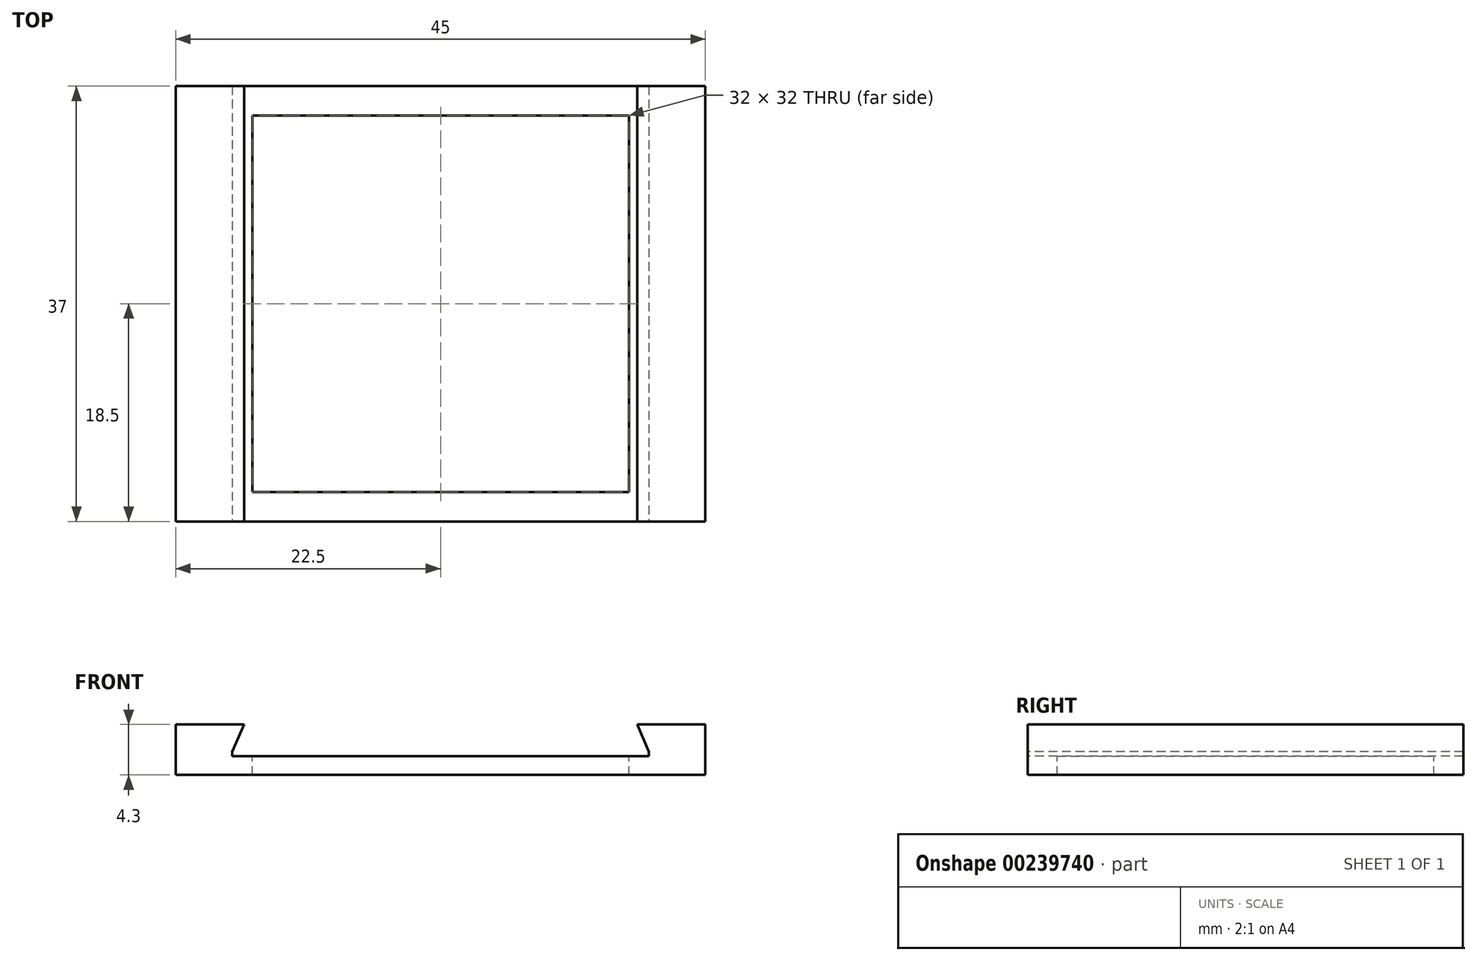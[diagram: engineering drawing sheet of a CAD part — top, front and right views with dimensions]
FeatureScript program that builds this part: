
annotation { "Feature Type Name" : "Feature", "Feature Type Description" : "" }
export const myFeature = defineFeature(function(context is Context, id is Id, definition is map)
    precondition{}
    {
        {
            var Q0;
            Q0=qCreatedBy(makeId("Top.planeOp"),FACE);
            var sketch = newSketch(context, id + "F0", { "sketchPlane" : qUnion([Q0])});
            skLineSegment(sketch, "E0.bottom", {"start": v(22.5, -18.5) * mm, "end": v(-22.5, -18.5) * mm});
            skLineSegment(sketch, "E0.top", {"start": v(22.5, 18.5) * mm, "end": v(-22.5, 18.5) * mm});
            skLineSegment(sketch, "E0.left", {"start": v(22.5, -18.5) * mm, "end": v(22.5, 18.5) * mm});
            skLineSegment(sketch, "E0.right", {"start": v(-22.5, -18.5) * mm, "end": v(-22.5, 18.5) * mm});
            skPoint(sketch, "E0.middle", {"position": v(0, 0) * mm});
            skSolve(sketch);
        }
        {
            var Q0;
            Q0=qSketchRegion(id+"F0",true);
            extrude(context, id + "F1", {"entities" : qUnion([Q0]), "depth" : 8 * mm});
        }
        {
            var Q0;
            Q0=makeQuery(id+"F1.opExtrude","SWEPT_FACE",FACE,{"disambiguationData":[OSD([sQuery(id+"F0.wireOp",EDGE,"E0.bottom")])]});
            var sketch = newSketch(context, id + "F2", { "sketchPlane" : qUnion([Q0])});
            skLineSegment(sketch, "E1", {"start": v(-22.5, 3) * mm, "end": v(22.5, 3) * mm, "construction": true});
            skLineSegment(sketch, "E2", {"start": v(-17.7, 8) * mm, "end": v(-17.7, 0) * mm, "construction": true});
            skLineSegment(sketch, "E3", {"start": v(0, 13.1) * mm, "end": v(0, -6.27) * mm, "construction": true});
            skLineSegment(sketch, "E4.MirrorCS", {"start": v(17.7, 8) * mm, "end": v(17.7, 0) * mm, "construction": true});
            skLineSegment(sketch, "E5", {"start": v(-15.7, 8) * mm, "end": v(-15.7, 0) * mm, "construction": true});
            skLineSegment(sketch, "E6", {"start": v(-15.7, 8) * mm, "end": v(15.7, 8) * mm});
            skLineSegment(sketch, "E7", {"start": v(-17.7, 3) * mm, "end": v(17.7, 3) * mm});
            skLineSegment(sketch, "E8", {"start": v(-17.7, 3) * mm, "end": v(-17.7, 3.4) * mm});
            skLineSegment(sketch, "E9", {"start": v(-17.7, 3.4) * mm, "end": v(-15.7, 8) * mm});
            skLineSegment(sketch, "E10.MirrorCS", {"start": v(17.7, 3.4) * mm, "end": v(15.7, 8) * mm});
            skLineSegment(sketch, "E11", {"start": v(17.7, 3.4) * mm, "end": v(17.7, 3) * mm});
            skSolve(sketch);
        }
        {
            var Q0;
            Q0=qSketchRegion(id+"F2",true);
            extrude(context, id + "F3", {"entities" : qUnion([Q0]), "operationType" : NewBodyOperationType.REMOVE, "endBound" : BoundingType.THROUGH_ALL, "oppositeDirection" : true, "depth" : 25 * mm});
        }
        {
            var Q0;
            Q0=makeQuery(id+"F2.imprint","IMPRINT",FACE,{"disambiguationData":[TD([[makeQuery(id+"F2.imprint","IMPRINT",EDGE,{"derivedFrom":sQuery(id+"F2.wireOp",EDGE,"E7")}),-1.0]])]});
            var sketch = newSketch(context, id + "F4", { "sketchPlane" : qUnion([Q0])});
            skLineSegment(sketch, "E12.bottom", {"start": v(-22.57, 0) * mm, "end": v(22.58, 0) * mm});
            skLineSegment(sketch, "E12.top", {"start": v(-22.57, 1.4) * mm, "end": v(22.58, 1.4) * mm});
            skLineSegment(sketch, "E12.left", {"start": v(-22.57, 0) * mm, "end": v(-22.57, 1.4) * mm});
            skLineSegment(sketch, "E12.right", {"start": v(22.58, 0) * mm, "end": v(22.58, 1.4) * mm});
            skLineSegment(sketch, "E13.bottom", {"start": v(-22.57, 8.1) * mm, "end": v(22.62, 8.1) * mm});
            skLineSegment(sketch, "E13.top", {"start": v(-22.57, 5.7) * mm, "end": v(22.62, 5.7) * mm});
            skLineSegment(sketch, "E13.left", {"start": v(-22.57, 8.1) * mm, "end": v(-22.57, 5.7) * mm});
            skLineSegment(sketch, "E13.right", {"start": v(22.62, 8.1) * mm, "end": v(22.62, 5.7) * mm});
            skSolve(sketch);
        }
        {
            var Q0;
            Q0 = qSketchRegion(id + "F4", true);
            extrude(context, id + "F5", {"entities" : qUnion([Q0]), "operationType" : NewBodyOperationType.REMOVE, "endBound" : BoundingType.THROUGH_ALL, "oppositeDirection" : true, "depth" : 25 * mm});
        }
        {
            var Q0;
            Q0=makeQuery(id+"F3.boolean.opBoolean","COPY",FACE,{"derivedFrom":makeQuery(id+"F3.opExtrude","SWEPT_FACE",FACE,{"disambiguationData":[OSD([sQuery(id+"F2.wireOp",EDGE,"E7")])]})});
            var sketch = newSketch(context, id + "F6", { "sketchPlane" : qUnion([Q0])});
            skLineSegment(sketch, "E14.bottom", {"start": v(16, -16) * mm, "end": v(-16, -16) * mm});
            skLineSegment(sketch, "E14.top", {"start": v(16, 16) * mm, "end": v(-16, 16) * mm});
            skLineSegment(sketch, "E14.left", {"start": v(16, -16) * mm, "end": v(16, 16) * mm});
            skLineSegment(sketch, "E14.right", {"start": v(-16, -16) * mm, "end": v(-16, 16) * mm});
            skPoint(sketch, "E14.middle", {"position": v(0, 0) * mm});
            skSolve(sketch);
        }
        {
            var Q0;
            Q0 = qSketchRegion(id + "F6", true);
            extrude(context, id + "F7", {"entities" : qUnion([Q0]), "operationType" : NewBodyOperationType.REMOVE, "endBound" : BoundingType.THROUGH_ALL, "oppositeDirection" : true, "depth" : 25 * mm});
        }
    });
